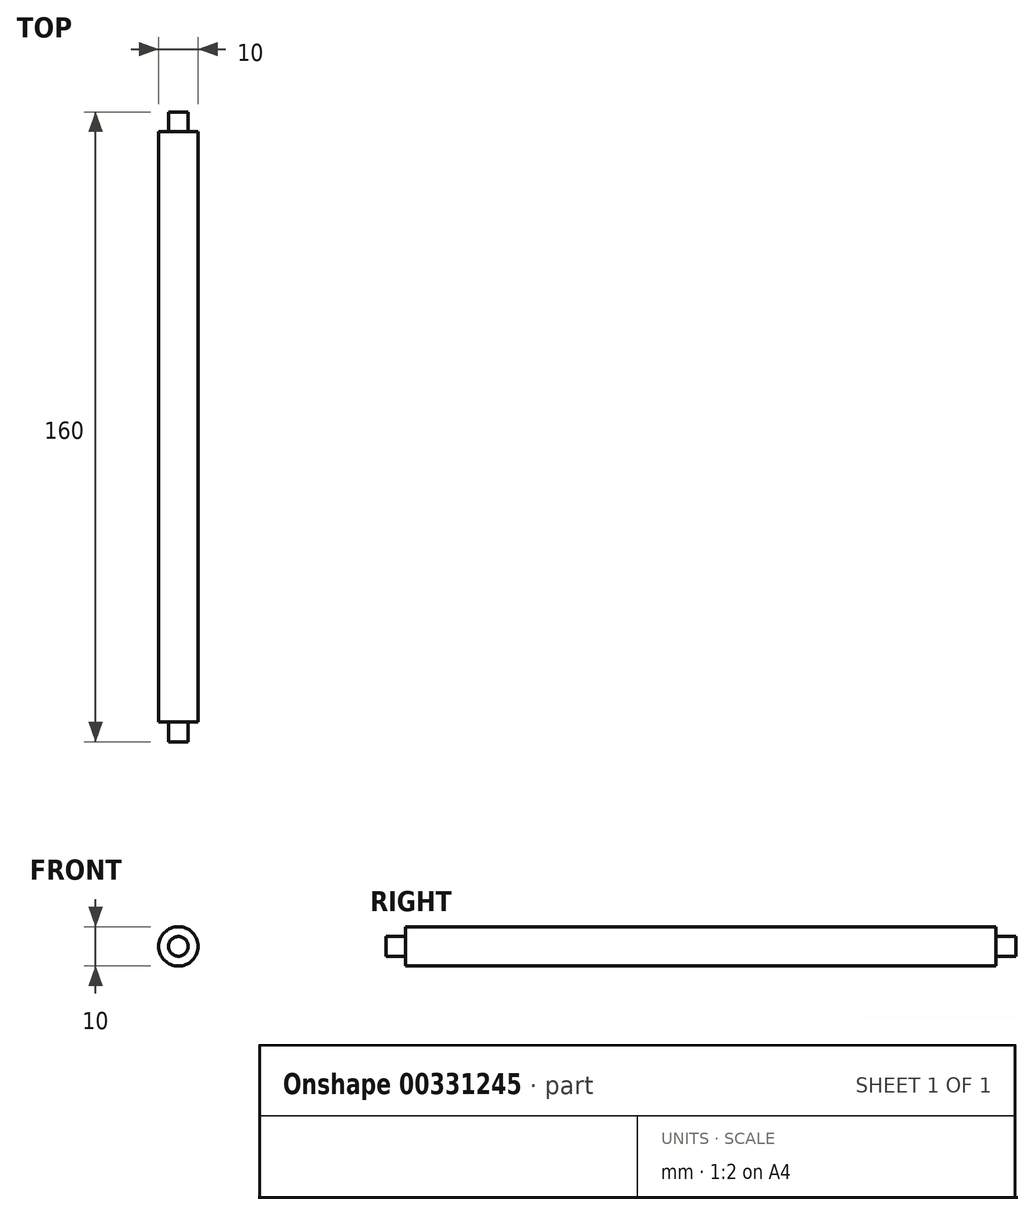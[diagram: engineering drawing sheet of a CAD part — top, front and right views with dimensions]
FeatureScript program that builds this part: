
annotation { "Feature Type Name" : "Feature", "Feature Type Description" : "" }
export const myFeature = defineFeature(function(context is Context, id is Id, definition is map)
    precondition{}
    {
        {
            var Q0;
            Q0=qCreatedBy(makeId("Front.planeOp"),FACE);
            var sketch = newSketch(context, id + "F0", { "sketchPlane" : qUnion([Q0])});
            skCircle(sketch, "E0", {"center": v(0, 0) * mm, "radius": 5 * mm});
            skSolve(sketch);
        }
        {
            var Q0;
            Q0 = qSketchRegion(id + "F0", true);
            extrude(context, id + "F1", {"entities" : qUnion([Q0]), "depth" : 150 * mm});
        }
        {
            var Q0;
            Q0=qCreatedBy(makeId("Front.planeOp"),FACE);
            var sketch = newSketch(context, id + "F2", { "sketchPlane" : qUnion([Q0])});
            skCircle(sketch, "E1", {"center": v(0, 0) * mm, "radius": 2.5 * mm});
            skSolve(sketch);
        }
        {
            var Q0;
            Q0 = qSketchRegion(id + "F2", true);
            extrude(context, id + "F3", {"entities" : qUnion([Q0]), "operationType" : NewBodyOperationType.ADD, "oppositeDirection" : true, "depth" : 5 * mm});
        }
        {
            var Q0;
            Q0=qCreatedBy(makeId("Front.planeOp"),FACE);
            var sketch = newSketch(context, id + "F4", { "sketchPlane" : qUnion([Q0])});
            skCircle(sketch, "E2", {"center": v(0, 0) * mm, "radius": 2.5 * mm});
            skSolve(sketch);
        }
        {
            var Q0;
            Q0 = qSketchRegion(id + "F4", true);
            extrude(context, id + "F5", {"entities" : qUnion([Q0]), "operationType" : NewBodyOperationType.ADD, "depth" : 155 * mm});
        }
    });
